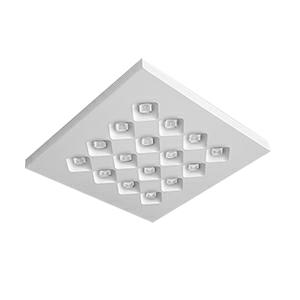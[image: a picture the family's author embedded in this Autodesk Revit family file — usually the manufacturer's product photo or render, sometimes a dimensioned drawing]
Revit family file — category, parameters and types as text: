
# Revit family: 3f_filippi_-_3f_diagon_3f_filippi_-_23028_a0686_-_3f_diagon_19w-840_dali_596x596___corn_plaf__f31e
name_source: partatom
category: Lighting Fixtures
units: mm (PartAtom-declared; Revit-internal decimal feet)

## family parameters
Cut with Voids When Loaded = No
Host = Face
Light Source = No
Part Type = Normal
Room Calculation Point = No
Round Connector Dimension = Use Diameter
Shared = No

## types (1)
- 3F Filippi - 3F Dìagon (1 x LED, 3354 lm, 21 W, 4000 K)
    Apparent Load = 21 VA
    Approval mark = CE
    CIE Flux Codes = 67 96 100 100 100
    Color Rendering = 80
    Color Temperature = 4000 K
    Control Gear = Electronic transformer
    Default Elevation = 1800 mm
    Description = ILLUMINOTECHNICAL
Luminous efficiency 100% (DLOR 100%, ULOR 0%).
Initial luminous flux of the luminaire 3354 lm.
Direct symmetric distribution.
Installation Interdistance Transv.D = 1.39 x hu - Long.D = 1.39 x hu.
Average luminance <1000 cd/m² for radial angles >65°.
Tabular UGR (CIE 117 - 4H-8H; S=0.25H; 70/50/20): RUG 16.5 - 16.5.
Beam angle: 93° - 92°.
Luminous efficacy 160 lm/W.
Lifetime (L95/B10): 30000 h. (tq+25°C)
Lifetime (L90/B10): 50000 h. (tq+25°C)
Lifetime (L80/B10): 80000 h. (tq+25°C)
Lifetime (L75/B10): 100000 h. (tq+25°C)
Sudden decreased luminous flux after 50000 hours: 0% (C0).
Photobiological safety in compliance with IEC/TR 62778: RG0 risk exempt, (IEC 62471).
In compliance with IEC/EN 62722-2-1 - IEC/EN 62717 standards.

SOURCE
Squared LED module 19W/840.
Energy efficiency class (UE 2019/2020 - UE 2019/2015): C.
CIE 13.3 Colour rendering index: CRI >80 (R9 <50%).
IES TM-30 Fidelity Index: Rf = 84 Rg = 95.
CCT nominal colour temperature 4000 K.
Colour initial tolerance (MacAdam): SDCM 3.

MECHANICAL
Housing in hot-galvanised steel, painted in white polyester.
Honeycombed diagonal screen in white anti-glare polycarbonate.
Rhomboidal lenses with differentiated surfaces, etched and prismatic to optimise the orientation of the luminous flux, in transparent methacrylate (PMMA).
Luminaire with limited surface temperature. - D - (EN 60598-2-24)
Dimensions: 600x600 mm, height 40 mm. Weight 6.115 kg.
IP43 protection degree for exposed part, IP20 for recessed part.
Mechanical strength to impacts IK06 (1 joule).
Glow-wire test resistance 650°C.

ELECTRICAL
Halogen Free DALI-2, PUSH-DIM, electronic wiring 230V-50/60Hz, power factor 0.90 at full load, THD <25%, constant output current, class I, 1 driver, 1 DALI addresse.
Power of the luminaire 21 W.
ENEC - CE.
SAFE FLICKER: PstLM=<1 and SVM=<0.4 (IEC TR 61547-1 and IEC TR 63158), to ensure a more comfortable and safe light.
Luminaire compliant with EN 60598-2-22 for power supply from a centralised emergency system CPSS (Central Power Supply System), not incorporated in the luminaire - high risk areas excluded. The default power and flux are 100% in AC and 15% in DC.
Ambient temperature from 0°C to +25°C.
Temperature class T6 max 85°C.
Quick connection.
Relative humidity UR: <85%.

INSTALLATION
Ceiling.
Height only 40 mm.
All accessories dedicated to this product are available on the Catalog and on our website www.3F-Filippi.com.

ACCESSORIES
A0686 - 596x596 Diagon frame for Ceiling installation.

APPLICATIONS
Environments: staterooms, with VDTs, offices.
Environments with exacting visual tasks, where diffused soft light for optimum visual comfort is required.

LIGHT MANAGEMENT
Recommended minimum setting: 10%.
The device, equipped with DALI-2 driver, can be controlled manually with 3F Easy Dim technology or automatically/manually with 3F Smart Dimming technology and/or centralised DALI systems.
DALI-2 certification guarantees interoperability with other devices with the same certification.
In electrical systems without a regulation system (manual or automatic) and DALI bus, a suitable jumper must be made on the DA-DA terminals of the appliance.

WARNING
Luminaire designed for disposal/recycling at end-of-life.
Replaceable (LED only) light source by a professional. Replaceable control gear by a professional.
    Height = 0 mm  [stored 0 ft]
    Lamp = 1 x LED
    Lamp Light Flux = 3354 lm
    Lamp Power = 21 W
    Lamp count = 1
    Length = 600 mm
    Lifetime = 50000 h
    Luminous efficacy = 160 lm/W
    Manufacturer = 3F Filippi
    ModVariant = No
    Model = 3F Filippi - 23028+A0686 - 3F Diagon 19W-840 DALI 596x596 + Corn.plaf.
    Mounting Place = Ceiling
    Mounting Type = Recessed
    Number of Poles = 1
    OnlyDefault = Yes
    Power Factor = 1
    Product Name = 3F Filippi - 3F Dìagon
    Product group = recessed luminaire
    ProductGroupID = 4
    Protection Class = Protection class I
    Protection Degree = IP 20
    RLX_Detail_Level = 1
    RLX_Emergency_Light_Flux = 0 lm
    RLX_Emergency_Type = 0
    RLX_Emergency_Type_DB = No
    RlxData = <blob elided: 97841 chars, md5=f1242c26>
    Socket = socket
    Standby Power = 0 W
    System Light Flux = 3354 lm
    System Power = 21 W
    Type Comments = Product without accessories
    Type Image = 3ffilippi_3f_diagon__a0686.jpg
    URL = http://relux.com
    VarID = ---
    Voltage = 0 V
    Weight = 0.00 kg
    Width = 600 mm

note: [stored X ft] marks values corroborated as IEEE doubles in the binary element streams (Revit-internal decimal feet)

## geometry (parser evidence)
native form markers: Blend x4, Sweep x9
no freeform markers — native parametric forms only
